# Revit family: SE-SU-420_GENERADO
name_source: partatom
category: Equipos mecánicos
revit_build: Autodesk Revit 2014 (Build: 20130308_1515(x64)
units: mm (PartAtom-declared; Revit-internal decimal feet)

## types (18) — shared parameters
Depth = 529 mm  [stored 1.73556 ft]
Fabricante = SAMMIC S.L.
Foodservice Equipment Identifier = Sí
Height = 448 mm  [stored 1.46982 ft]
Revision Code = 1
URL = https://www.sammic.com
Width = 484 mm  [stored 1.58793 ft]

## per-type parameters (varying)
| type | Comentarios de tipo | Cycle | FL Amps | Modelo | Specification by Manufacturer | URL Cutsheet | Volts | Weight in Pounds |
| Vacuum packing machine SE-416 230/50-60/1 | Tabletop model. 16 m³/h. 420 mm. | 50 Hz | 4 A | 1140636 | 420 mm. sealing bar.
16 m³/h Busch vacuum pump.
Vacuum controlled by sensor. | http://www.sammic.com | 230 V | 143.3 |
| Vacuum packing machine SE-416 120/50-60/1 | Tabletop model. 16 m³/h. 420 mm. | 60 Hz | 8 A | 1140637 | 420 mm. sealing bar.
16 m³/h Busch vacuum pump.
Vacuum controlled by sensor. | http://www.sammic.com | 120 V | 143.3 |
| Vacuum packing machine SE-420 230/50-60/1 | Tabletop model. 20 m³/h. 420 mm. | 50 Hz | 5 A | 1140638 | 420 mm. sealing bar.
20 m³/h Busch vacuum pump.
Vacuum controlled by sensor. | http://www.sammic.com | 230 V | 154.3 |
| Vacuum packing machine SE-420 120/50-60/1 | Tabletop model. 20 m³/h. 420 mm. | 60 Hz | 13 A | 1140639 | 420 mm. sealing bar.
20 m³/h Busch vacuum pump.
Vacuum controlled by sensor. | http://www.sammic.com | 120 V | 154.3 |
| Vacuum packing machine SE-420 230/50-60/1 KSA | Tabletop model. 20 m³/h. 420 mm. | 50 Hz | 5 A | 1140646 | 420 mm. sealing bar.
20 m³/h Busch vacuum pump.
Vacuum controlled by sensor. |  | 230 V | 154.3 |
| Vacuum packing machine SU-416 230/50-60/1 | Tabletop model. 16 m³/h. 420 mm. | 50 Hz | 4 A | 1140760 | 420 mm. sealing bar.
16 m³/h Busch vacuum pump.
Vacuum controlled by sensor. | http://www.sammic.com | 230 V | 143.3 |
| Vacuum packing machine SU-416P 230/50-60/1 | Tabletop model. 16 m³/h. 420 mm. | 50 Hz | 4 A | 1140762 | 420 mm. sealing bar.
16 m³/h Busch vacuum pump.
Vacuum controlled by sensor. | http://www.sammic.com | 230 V | 143.3 |
| Vacuum packing machine SU-416 120/50-60/1 | Tabletop model. 16 m³/h. 420 mm. | 60 Hz | 8 A | 1140765 | 420 mm. sealing bar.
16 m³/h Busch vacuum pump.
Vacuum controlled by sensor. | http://www.sammic.com | 120 V | 143.3 |
| Vacuum packing machine SU-416P 120/50-60/1 | Tabletop model. 16 m³/h. 420 mm. | 60 Hz | 8 A | 1140767 | 420 mm. sealing bar.
16 m³/h Busch vacuum pump.
Vacuum controlled by sensor. | http://www.sammic.com | 120 V | 143.3 |
| Vacuum packing machine SU-416 230/50-60/1 KSA | Tabletop model. 16 m³/h. 420 mm. | 50 Hz | 4 A | 1140764 | 420 mm. sealing bar.
16 m³/h Busch vacuum pump.
Vacuum controlled by sensor. |  | 230 V | 143.3 |
| Vacuum packing machine SU-420 230/50-60/1 | Tabletop model. 20 m³/h. 420 mm. | 50 Hz | 5 A | 1140772 | 420 mm. sealing bar.
20 m³/h Busch vacuum pump.
Vacuum controlled by sensor. | http://www.sammic.com | 230 V | 154.3 |
| Vacuum packing machine SU-420P 230/50-60/1 | Tabletop model. 20 m³/h. 420 mm. | 50 Hz | 5 A | 1140774 | 420 mm. sealing bar.
20 m³/h Busch vacuum pump.
Vacuum controlled by sensor. | http://www.sammic.com | 230 V | 154.3 |
| Vacuum packing machine SU-420+ 230/50-60/1 | Tabletop model. 20 m³/h. 420 mm. | 50 Hz | 5 A | 1140775 | 420 mm. sealing bar.
20 m³/h Busch vacuum pump.
Vacuum controlled by sensor. | http://www.sammic.com | 230 V | 154.3 |
| Vacuum packing machine SU-420P+ 230/50-60/1 | Tabletop model. 20 m³/h. 420 mm. | 50 Hz | 5 A | 1140776 | 420 mm. sealing bar.
20 m³/h Busch vacuum pump.
Vacuum controlled by sensor. | http://www.sammic.com | 230 V | 154.3 |
| Vacuum packing machine SU-420 120/50-60/1 | Tabletop model. 20 m³/h. 420 mm. | 60 Hz | 13 A | 1140781 | 420 mm. sealing bar.
20 m³/h Busch vacuum pump.
Vacuum controlled by sensor. | http://www.sammic.com | 120 V | 154.3 |
| Vacuum packing machine SU-420P 120/50-60/1 | Tabletop model. 20 m³/h. 420 mm. | 60 Hz | 13 A | 1140783 | 420 mm. sealing bar.
20 m³/h Busch vacuum pump.
Vacuum controlled by sensor. | http://www.sammic.com | 120 V | 154.3 |
| Vacuum packing machine SU-420+ 120/50-60/1 | Tabletop model. 20 m³/h. 420 mm. | 60 Hz | 13 A | 1140784 | 420 mm. sealing bar.
20 m³/h Busch vacuum pump.
Vacuum controlled by sensor. | http://www.sammic.com | 120 V | 154.3 |
| Vacuum packing machine SU-420P+ 120/50-60/1 (with PLUS welding option) | Tabletop model. 20 m³/h. 420 mm. | 60 Hz | 13 A | 1140785 | 420 mm. sealing bar.
20 m³/h Busch vacuum pump.
Vacuum controlled by sensor. | http://www.sammic.com | 120 V | 154.3 |

note: column(s) folded — value = type name in every type: Descripción

note: [stored X ft] marks values corroborated as IEEE doubles in the binary element streams (Revit-internal decimal feet)
